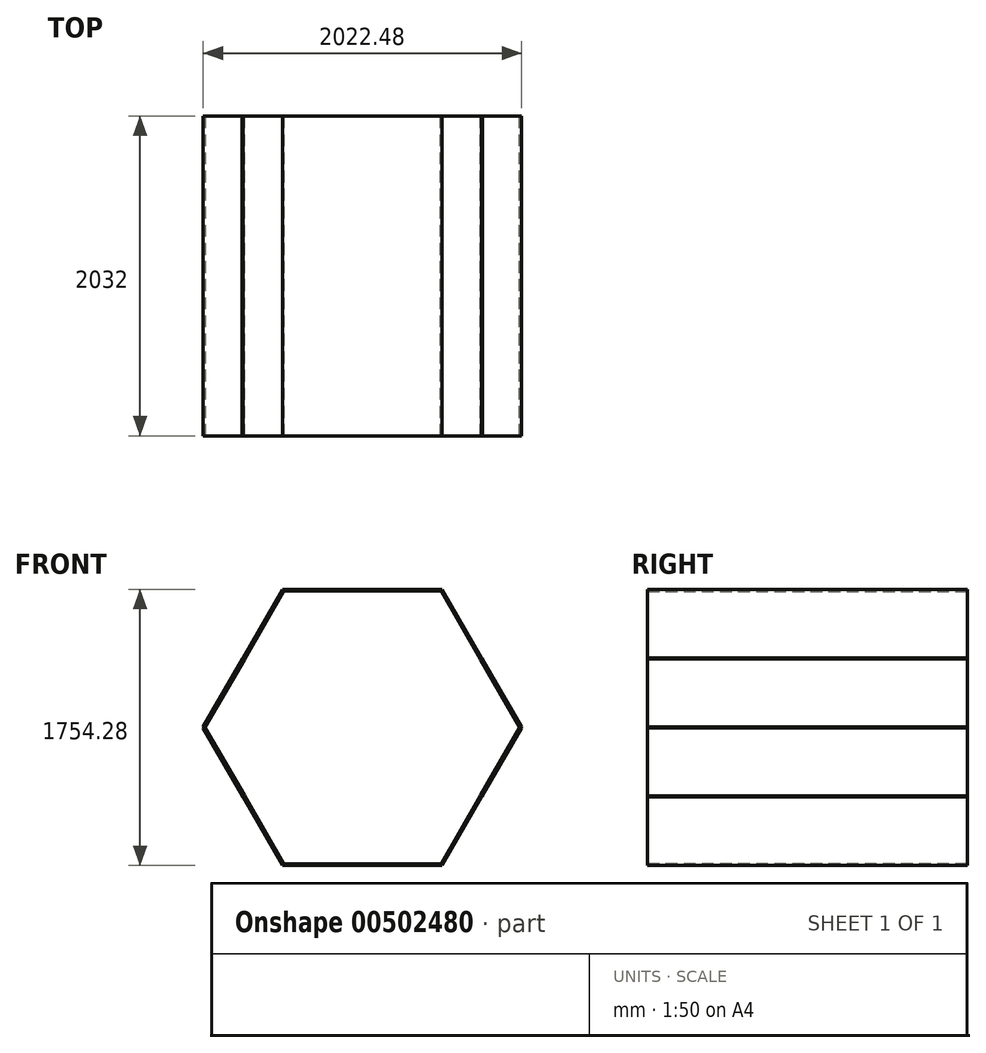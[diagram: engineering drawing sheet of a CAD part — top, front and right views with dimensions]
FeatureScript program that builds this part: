
annotation { "Feature Type Name" : "Feature", "Feature Type Description" : "" }
export const myFeature = defineFeature(function(context is Context, id is Id, definition is map)
    precondition{}
    {
        {
            var Q0;
            Q0=qCreatedBy(makeId("Front.planeOp"),FACE);
            var sketch = newSketch(context, id + "F0", { "sketchPlane" : qUnion([Q0])});
            skCircle(sketch, "E0.cCircle", {"center": v(0, 0) * mm, "radius": 866.03 * mm, "construction": true});
            skLineSegment(sketch, "E0.0", {"start": v(500, -866.03) * mm, "end": v(-500, -866.03) * mm});
            skLineSegment(sketch, "E0.1", {"start": v(-500, -866.03) * mm, "end": v(-1000, 0) * mm});
            skLineSegment(sketch, "E0.2", {"start": v(-1000, 0) * mm, "end": v(-500, 866.03) * mm});
            skLineSegment(sketch, "E0.3", {"start": v(-500, 866.03) * mm, "end": v(500, 866.03) * mm});
            skLineSegment(sketch, "E0.4", {"start": v(500, 866.03) * mm, "end": v(1000, 0) * mm});
            skLineSegment(sketch, "E0.5", {"start": v(1000, 0) * mm, "end": v(500, -866.03) * mm});
            skPoint(sketch, "E0.0.midPoint", {"position": v(0, -866.03) * mm});
            skCircle(sketch, "E1.cCircle", {"center": v(0, 0) * mm, "radius": 877.14 * mm, "construction": true});
            skLineSegment(sketch, "E1.0", {"start": v(506.42, -877.14) * mm, "end": v(-506.42, -877.14) * mm});
            skLineSegment(sketch, "E1.1", {"start": v(-506.42, -877.14) * mm, "end": v(-1012.83, 0) * mm});
            skLineSegment(sketch, "E1.2", {"start": v(-1012.83, 0) * mm, "end": v(-506.42, 877.14) * mm});
            skLineSegment(sketch, "E1.3", {"start": v(-506.42, 877.14) * mm, "end": v(506.42, 877.14) * mm});
            skLineSegment(sketch, "E1.4", {"start": v(506.42, 877.14) * mm, "end": v(1012.83, 0) * mm});
            skLineSegment(sketch, "E1.5", {"start": v(1012.83, 0) * mm, "end": v(506.42, -877.14) * mm});
            skPoint(sketch, "E1.0.midPoint", {"position": v(0, -877.14) * mm});
            skLineSegment(sketch, "E2", {"start": v(-506.42, 877.14) * mm, "end": v(-500, 866.03) * mm});
            skLineSegment(sketch, "E3", {"start": v(500, 866.03) * mm, "end": v(506.42, 877.14) * mm});
            skLineSegment(sketch, "E4", {"start": v(1000, 0) * mm, "end": v(1012.83, 0) * mm});
            skLineSegment(sketch, "E5", {"start": v(500, -866.03) * mm, "end": v(506.42, -877.14) * mm});
            skLineSegment(sketch, "E6", {"start": v(-506.42, -877.14) * mm, "end": v(-500, -866.03) * mm});
            skLineSegment(sketch, "E7", {"start": v(-1012.83, 0) * mm, "end": v(-1000, 0) * mm});
            skLineSegment(sketch, "E8", {"start": v(-759.62, 438.57) * mm, "end": v(-750, 433.01) * mm});
            skLineSegment(sketch, "E9", {"start": v(750, 433.01) * mm, "end": v(759.62, 438.57) * mm});
            skLineSegment(sketch, "E10", {"start": v(750, -433.01) * mm, "end": v(759.62, -438.57) * mm});
            skLineSegment(sketch, "E11", {"start": v(-759.62, -438.57) * mm, "end": v(-750, -433.01) * mm});
            skCircle(sketch, "E12", {"center": v(-759.62, 438.57) * mm, "radius": 3.18 * mm});
            skCircle(sketch, "E13", {"center": v(-759.62, -438.57) * mm, "radius": 3.18 * mm});
            skCircle(sketch, "E14", {"center": v(-1012.83, 0) * mm, "radius": 3.18 * mm});
            skCircle(sketch, "E15", {"center": v(-500, -866.03) * mm, "radius": 3.18 * mm});
            skCircle(sketch, "E16", {"center": v(500, -866.03) * mm, "radius": 3.18 * mm});
            skCircle(sketch, "E17", {"center": v(759.62, -438.57) * mm, "radius": 3.18 * mm});
            skCircle(sketch, "E18", {"center": v(1012.83, 0) * mm, "radius": 3.18 * mm});
            skCircle(sketch, "E19", {"center": v(759.62, 438.57) * mm, "radius": 3.18 * mm});
            skCircle(sketch, "E20", {"center": v(500, 866.03) * mm, "radius": 3.18 * mm});
            skCircle(sketch, "E21", {"center": v(-1000, 0) * mm, "radius": 3.18 * mm});
            skCircle(sketch, "E22", {"center": v(1000, 0) * mm, "radius": 3.18 * mm});
            skCircle(sketch, "E23", {"center": v(-500, 866.03) * mm, "radius": 3.18 * mm});
            skSolve(sketch);
        }
        {
            var Q0;
            {var subQ1=sQuery(id+"F0.wireOp",EDGE,"E1.0");Q0=makeQuery(id+"F0.imprint","IMPRINT",FACE,{"disambiguationData":[TD([[makeQuery(id+"F0.imprint","IMPRINT",EDGE,{"derivedFrom":subQ1}),-1.0]])]});}
            var Q1;
            {var subQ0=sQuery(id+"F0.wireOp",EDGE,"E10");var subQ1=sQuery(id+"F0.wireOp",EDGE,"E0.5");var subQ2=makeQuery(id+"F0.imprint","INTERSECT",VERTEX,{"derivedFrom":[subQ1,subQ0]});Q1=makeQuery(id+"F0.imprint","IMPRINT",FACE,{"disambiguationData":[TD([[makeQuery(id+"F0.imprint","IMPRINT",EDGE,{"disambiguationData":[TD([[subQ2,1.0]])],"derivedFrom":subQ1}),1.0]])]});}
            var Q2;
            {var subQ5=sQuery(id+"F0.wireOp",EDGE,"E9");var subQ6=sQuery(id+"F0.wireOp",EDGE,"E0.4");var subQ7=makeQuery(id+"F0.imprint","INTERSECT",VERTEX,{"derivedFrom":[subQ6,subQ5]});Q2=makeQuery(id+"F0.imprint","IMPRINT",FACE,{"disambiguationData":[TD([[makeQuery(id+"F0.imprint","IMPRINT",EDGE,{"disambiguationData":[TD([[subQ7,1.0]])],"derivedFrom":subQ6}),1.0]])]});}
            var Q3;
            {var subQ0=sQuery(id+"F0.wireOp",EDGE,"E11");var subQ1=sQuery(id+"F0.wireOp",EDGE,"E0.1");var subQ2=makeQuery(id+"F0.imprint","INTERSECT",VERTEX,{"derivedFrom":[subQ1,subQ0]});Q3=makeQuery(id+"F0.imprint","IMPRINT",FACE,{"disambiguationData":[TD([[makeQuery(id+"F0.imprint","IMPRINT",EDGE,{"disambiguationData":[TD([[subQ2,-1.0]])],"derivedFrom":subQ1}),1.0]])]});}
            var Q4;
            {var subQ5=sQuery(id+"F0.wireOp",EDGE,"E8");var subQ6=sQuery(id+"F0.wireOp",EDGE,"E0.2");var subQ7=makeQuery(id+"F0.imprint","INTERSECT",VERTEX,{"derivedFrom":[subQ6,subQ5]});Q4=makeQuery(id+"F0.imprint","IMPRINT",FACE,{"disambiguationData":[TD([[makeQuery(id+"F0.imprint","IMPRINT",EDGE,{"disambiguationData":[TD([[subQ7,-1.0]])],"derivedFrom":subQ6}),1.0]])]});}
            extrude(context, id + "F1", {"entities" : qUnion([Q0, Q1, Q2, Q3, Q4]), "depth" : 2032 * mm, "offsetDistance" : 25.4 * mm});
        }
        {
            var Q0;
            {var subQ0=sQuery(id+"F0.wireOp",EDGE,"E9");var subQ1=sQuery(id+"F0.wireOp",EDGE,"E0.4");var subQ2=makeQuery(id+"F0.imprint","INTERSECT",VERTEX,{"derivedFrom":[subQ1,subQ0]});Q0=makeQuery(id+"F0.imprint","IMPRINT",FACE,{"disambiguationData":[TD([[makeQuery(id+"F0.imprint","IMPRINT",EDGE,{"disambiguationData":[TD([[subQ2,-1.0]])],"derivedFrom":subQ1}),1.0]])]});}
            var Q1;
            {var subQ1=sQuery(id+"F0.wireOp",EDGE,"E1.3");Q1=makeQuery(id+"F0.imprint","IMPRINT",FACE,{"disambiguationData":[TD([[makeQuery(id+"F0.imprint","IMPRINT",EDGE,{"derivedFrom":subQ1}),-1.0]])]});}
            var Q2;
            {var subQ0=sQuery(id+"F0.wireOp",EDGE,"E8");var subQ1=sQuery(id+"F0.wireOp",EDGE,"E0.2");var subQ2=makeQuery(id+"F0.imprint","INTERSECT",VERTEX,{"derivedFrom":[subQ1,subQ0]});Q2=makeQuery(id+"F0.imprint","IMPRINT",FACE,{"disambiguationData":[TD([[makeQuery(id+"F0.imprint","IMPRINT",EDGE,{"disambiguationData":[TD([[subQ2,1.0]])],"derivedFrom":subQ1}),1.0]])]});}
            var Q3;
            {var subQ0=sQuery(id+"F0.wireOp",EDGE,"E11");var subQ1=sQuery(id+"F0.wireOp",EDGE,"E0.1");var subQ2=makeQuery(id+"F0.imprint","INTERSECT",VERTEX,{"derivedFrom":[subQ1,subQ0]});Q3=makeQuery(id+"F0.imprint","IMPRINT",FACE,{"disambiguationData":[TD([[makeQuery(id+"F0.imprint","IMPRINT",EDGE,{"disambiguationData":[TD([[subQ2,1.0]])],"derivedFrom":subQ1}),1.0]])]});}
            var Q4;
            {var subQ0=sQuery(id+"F0.wireOp",EDGE,"E10");var subQ1=sQuery(id+"F0.wireOp",EDGE,"E0.5");var subQ2=makeQuery(id+"F0.imprint","INTERSECT",VERTEX,{"derivedFrom":[subQ1,subQ0]});Q4=makeQuery(id+"F0.imprint","IMPRINT",FACE,{"disambiguationData":[TD([[makeQuery(id+"F0.imprint","IMPRINT",EDGE,{"disambiguationData":[TD([[subQ2,-1.0]])],"derivedFrom":subQ1}),1.0]])]});}
            extrude(context, id + "F2", {"entities" : qUnion([Q0, Q1, Q2, Q3, Q4]), "depth" : 2032 * mm, "offsetDistance" : 25.4 * mm});
        }
        {
            var Q0;
            {var subQ0=sQuery(id+"F0.wireOp",EDGE,"E1.1");var subQ1=makeQuery(id+"F0.imprint","INTERSECT",VERTEX,{"derivedFrom":[subQ0,sQuery(id+"F0.wireOp",EDGE,"E11")]});Q0=makeQuery(id+"F0.imprint","IMPRINT",FACE,{"disambiguationData":[TD([[makeQuery(id+"F0.imprint","IMPRINT",EDGE,{"disambiguationData":[TD([[subQ1,1.0]])],"derivedFrom":subQ0}),1.0]])]});}
            var Q1;
            {var subQ0=sQuery(id+"F0.wireOp",EDGE,"E11");var subQ1=sQuery(id+"F0.wireOp",EDGE,"E1.1");var subQ2=makeQuery(id+"F0.imprint","INTERSECT",VERTEX,{"derivedFrom":[subQ1,subQ0]});Q1=makeQuery(id+"F0.imprint","IMPRINT",FACE,{"disambiguationData":[TD([[makeQuery(id+"F0.imprint","IMPRINT",EDGE,{"disambiguationData":[TD([[subQ2,-1.0]])],"derivedFrom":subQ1}),-1.0]])]});}
            var Q2;
            {var subQ0=sQuery(id+"F0.wireOp",EDGE,"E11");var subQ1=sQuery(id+"F0.wireOp",EDGE,"E1.1");var subQ2=makeQuery(id+"F0.imprint","INTERSECT",VERTEX,{"derivedFrom":[subQ1,subQ0]});Q2=makeQuery(id+"F0.imprint","IMPRINT",FACE,{"disambiguationData":[TD([[makeQuery(id+"F0.imprint","IMPRINT",EDGE,{"disambiguationData":[TD([[subQ2,1.0]])],"derivedFrom":subQ1}),-1.0]])]});}
            var Q3;
            {var subQ1=sQuery(id+"F0.wireOp",EDGE,"E0.0");var subQ3=sQuery(id+"F0.wireOp",EDGE,"E15");var subQ4=makeQuery(id+"F0.imprint","INTERSECT",VERTEX,{"derivedFrom":[subQ1,subQ3]});Q3=makeQuery(id+"F0.imprint","IMPRINT",FACE,{"disambiguationData":[TD([[makeQuery(id+"F0.imprint","IMPRINT",EDGE,{"disambiguationData":[TD([[subQ4,-1.0]])],"derivedFrom":subQ3}),1.0]])]});}
            var Q4;
            {var subQ1=sQuery(id+"F0.wireOp",EDGE,"E0.0");var subQ3=sQuery(id+"F0.wireOp",EDGE,"E15");var subQ4=makeQuery(id+"F0.imprint","INTERSECT",VERTEX,{"derivedFrom":[subQ1,subQ3]});Q4=makeQuery(id+"F0.imprint","IMPRINT",FACE,{"disambiguationData":[TD([[makeQuery(id+"F0.imprint","IMPRINT",EDGE,{"disambiguationData":[TD([[subQ4,1.0]])],"derivedFrom":subQ3}),1.0]])]});}
            var Q5;
            {var subQ1=sQuery(id+"F0.wireOp",EDGE,"E0.1");var subQ3=sQuery(id+"F0.wireOp",EDGE,"E15");var subQ4=makeQuery(id+"F0.imprint","INTERSECT",VERTEX,{"derivedFrom":[subQ1,subQ3]});Q5=makeQuery(id+"F0.imprint","IMPRINT",FACE,{"disambiguationData":[TD([[makeQuery(id+"F0.imprint","IMPRINT",EDGE,{"disambiguationData":[TD([[subQ4,-1.0]])],"derivedFrom":subQ3}),1.0]])]});}
            var Q6;
            {var subQ1=sQuery(id+"F0.wireOp",EDGE,"E0.5");var subQ3=sQuery(id+"F0.wireOp",EDGE,"E16");var subQ4=makeQuery(id+"F0.imprint","INTERSECT",VERTEX,{"derivedFrom":[subQ1,subQ3]});Q6=makeQuery(id+"F0.imprint","IMPRINT",FACE,{"disambiguationData":[TD([[makeQuery(id+"F0.imprint","IMPRINT",EDGE,{"disambiguationData":[TD([[subQ4,1.0]])],"derivedFrom":subQ3}),1.0]])]});}
            var Q7;
            {var subQ1=sQuery(id+"F0.wireOp",EDGE,"E0.0");var subQ3=sQuery(id+"F0.wireOp",EDGE,"E16");var subQ4=makeQuery(id+"F0.imprint","INTERSECT",VERTEX,{"derivedFrom":[subQ1,subQ3]});Q7=makeQuery(id+"F0.imprint","IMPRINT",FACE,{"disambiguationData":[TD([[makeQuery(id+"F0.imprint","IMPRINT",EDGE,{"disambiguationData":[TD([[subQ4,1.0]])],"derivedFrom":subQ3}),1.0]])]});}
            var Q8;
            {var subQ1=sQuery(id+"F0.wireOp",EDGE,"E0.0");var subQ3=sQuery(id+"F0.wireOp",EDGE,"E16");var subQ4=makeQuery(id+"F0.imprint","INTERSECT",VERTEX,{"derivedFrom":[subQ1,subQ3]});Q8=makeQuery(id+"F0.imprint","IMPRINT",FACE,{"disambiguationData":[TD([[makeQuery(id+"F0.imprint","IMPRINT",EDGE,{"disambiguationData":[TD([[subQ4,-1.0]])],"derivedFrom":subQ3}),1.0]])]});}
            var Q9;
            {var subQ0=sQuery(id+"F0.wireOp",EDGE,"E10");var subQ1=sQuery(id+"F0.wireOp",EDGE,"E1.5");var subQ2=makeQuery(id+"F0.imprint","INTERSECT",VERTEX,{"derivedFrom":[subQ1,subQ0]});Q9=makeQuery(id+"F0.imprint","IMPRINT",FACE,{"disambiguationData":[TD([[makeQuery(id+"F0.imprint","IMPRINT",EDGE,{"disambiguationData":[TD([[subQ2,1.0]])],"derivedFrom":subQ1}),-1.0]])]});}
            var Q10;
            {var subQ0=sQuery(id+"F0.wireOp",EDGE,"E10");var subQ1=sQuery(id+"F0.wireOp",EDGE,"E1.5");var subQ2=makeQuery(id+"F0.imprint","INTERSECT",VERTEX,{"derivedFrom":[subQ1,subQ0]});Q10=makeQuery(id+"F0.imprint","IMPRINT",FACE,{"disambiguationData":[TD([[makeQuery(id+"F0.imprint","IMPRINT",EDGE,{"disambiguationData":[TD([[subQ2,-1.0]])],"derivedFrom":subQ1}),-1.0]])]});}
            var Q11;
            {var subQ0=sQuery(id+"F0.wireOp",EDGE,"E1.5");var subQ1=makeQuery(id+"F0.imprint","INTERSECT",VERTEX,{"derivedFrom":[subQ0,sQuery(id+"F0.wireOp",EDGE,"E10")]});Q11=makeQuery(id+"F0.imprint","IMPRINT",FACE,{"disambiguationData":[TD([[makeQuery(id+"F0.imprint","IMPRINT",EDGE,{"disambiguationData":[TD([[subQ1,1.0]])],"derivedFrom":subQ0}),1.0]])]});}
            var Q12;
            {var subQ1=sQuery(id+"F0.wireOp",EDGE,"E0.4");var subQ3=sQuery(id+"F0.wireOp",EDGE,"E22");var subQ4=makeQuery(id+"F0.imprint","INTERSECT",VERTEX,{"derivedFrom":[subQ1,subQ3]});Q12=makeQuery(id+"F0.imprint","IMPRINT",FACE,{"disambiguationData":[TD([[makeQuery(id+"F0.imprint","IMPRINT",EDGE,{"disambiguationData":[TD([[subQ4,1.0]])],"derivedFrom":subQ3}),1.0]])]});}
            var Q13;
            {var subQ1=sQuery(id+"F0.wireOp",EDGE,"E0.5");var subQ3=sQuery(id+"F0.wireOp",EDGE,"E22");var subQ4=makeQuery(id+"F0.imprint","INTERSECT",VERTEX,{"derivedFrom":[subQ1,subQ3]});Q13=makeQuery(id+"F0.imprint","IMPRINT",FACE,{"disambiguationData":[TD([[makeQuery(id+"F0.imprint","IMPRINT",EDGE,{"disambiguationData":[TD([[subQ4,-1.0]])],"derivedFrom":subQ3}),1.0]])]});}
            var Q14;
            {var subQ1=sQuery(id+"F0.wireOp",EDGE,"E0.4");var subQ3=sQuery(id+"F0.wireOp",EDGE,"E22");var subQ4=makeQuery(id+"F0.imprint","INTERSECT",VERTEX,{"derivedFrom":[subQ1,subQ3]});Q14=makeQuery(id+"F0.imprint","IMPRINT",FACE,{"disambiguationData":[TD([[makeQuery(id+"F0.imprint","IMPRINT",EDGE,{"disambiguationData":[TD([[subQ4,-1.0]])],"derivedFrom":subQ3}),1.0]])]});}
            var Q15;
            {var subQ0=sQuery(id+"F0.wireOp",EDGE,"E1.4");var subQ1=makeQuery(id+"F0.imprint","INTERSECT",VERTEX,{"derivedFrom":[subQ0,sQuery(id+"F0.wireOp",EDGE,"E9")]});Q15=makeQuery(id+"F0.imprint","IMPRINT",FACE,{"disambiguationData":[TD([[makeQuery(id+"F0.imprint","IMPRINT",EDGE,{"disambiguationData":[TD([[subQ1,1.0]])],"derivedFrom":subQ0}),1.0]])]});}
            var Q16;
            {var subQ0=sQuery(id+"F0.wireOp",EDGE,"E9");var subQ1=sQuery(id+"F0.wireOp",EDGE,"E1.4");var subQ2=makeQuery(id+"F0.imprint","INTERSECT",VERTEX,{"derivedFrom":[subQ1,subQ0]});Q16=makeQuery(id+"F0.imprint","IMPRINT",FACE,{"disambiguationData":[TD([[makeQuery(id+"F0.imprint","IMPRINT",EDGE,{"disambiguationData":[TD([[subQ2,-1.0]])],"derivedFrom":subQ1}),-1.0]])]});}
            var Q17;
            {var subQ0=sQuery(id+"F0.wireOp",EDGE,"E9");var subQ1=sQuery(id+"F0.wireOp",EDGE,"E1.4");var subQ2=makeQuery(id+"F0.imprint","INTERSECT",VERTEX,{"derivedFrom":[subQ1,subQ0]});Q17=makeQuery(id+"F0.imprint","IMPRINT",FACE,{"disambiguationData":[TD([[makeQuery(id+"F0.imprint","IMPRINT",EDGE,{"disambiguationData":[TD([[subQ2,1.0]])],"derivedFrom":subQ1}),-1.0]])]});}
            var Q18;
            {var subQ1=sQuery(id+"F0.wireOp",EDGE,"E0.3");var subQ3=sQuery(id+"F0.wireOp",EDGE,"E20");var subQ4=makeQuery(id+"F0.imprint","INTERSECT",VERTEX,{"derivedFrom":[subQ1,subQ3]});Q18=makeQuery(id+"F0.imprint","IMPRINT",FACE,{"disambiguationData":[TD([[makeQuery(id+"F0.imprint","IMPRINT",EDGE,{"disambiguationData":[TD([[subQ4,1.0]])],"derivedFrom":subQ3}),1.0]])]});}
            var Q19;
            {var subQ1=sQuery(id+"F0.wireOp",EDGE,"E0.3");var subQ3=sQuery(id+"F0.wireOp",EDGE,"E20");var subQ4=makeQuery(id+"F0.imprint","INTERSECT",VERTEX,{"derivedFrom":[subQ1,subQ3]});Q19=makeQuery(id+"F0.imprint","IMPRINT",FACE,{"disambiguationData":[TD([[makeQuery(id+"F0.imprint","IMPRINT",EDGE,{"disambiguationData":[TD([[subQ4,-1.0]])],"derivedFrom":subQ3}),1.0]])]});}
            var Q20;
            {var subQ1=sQuery(id+"F0.wireOp",EDGE,"E0.4");var subQ3=sQuery(id+"F0.wireOp",EDGE,"E20");var subQ4=makeQuery(id+"F0.imprint","INTERSECT",VERTEX,{"derivedFrom":[subQ1,subQ3]});Q20=makeQuery(id+"F0.imprint","IMPRINT",FACE,{"disambiguationData":[TD([[makeQuery(id+"F0.imprint","IMPRINT",EDGE,{"disambiguationData":[TD([[subQ4,-1.0]])],"derivedFrom":subQ3}),1.0]])]});}
            var Q21;
            {var subQ1=sQuery(id+"F0.wireOp",EDGE,"E0.2");var subQ3=sQuery(id+"F0.wireOp",EDGE,"E23");var subQ4=makeQuery(id+"F0.imprint","INTERSECT",VERTEX,{"derivedFrom":[subQ1,subQ3]});Q21=makeQuery(id+"F0.imprint","IMPRINT",FACE,{"disambiguationData":[TD([[makeQuery(id+"F0.imprint","IMPRINT",EDGE,{"disambiguationData":[TD([[subQ4,-1.0]])],"derivedFrom":subQ3}),1.0]])]});}
            var Q22;
            {var subQ1=sQuery(id+"F0.wireOp",EDGE,"E0.3");var subQ3=sQuery(id+"F0.wireOp",EDGE,"E23");var subQ4=makeQuery(id+"F0.imprint","INTERSECT",VERTEX,{"derivedFrom":[subQ1,subQ3]});Q22=makeQuery(id+"F0.imprint","IMPRINT",FACE,{"disambiguationData":[TD([[makeQuery(id+"F0.imprint","IMPRINT",EDGE,{"disambiguationData":[TD([[subQ4,-1.0]])],"derivedFrom":subQ3}),1.0]])]});}
            var Q23;
            {var subQ1=sQuery(id+"F0.wireOp",EDGE,"E0.2");var subQ3=sQuery(id+"F0.wireOp",EDGE,"E23");var subQ4=makeQuery(id+"F0.imprint","INTERSECT",VERTEX,{"derivedFrom":[subQ1,subQ3]});Q23=makeQuery(id+"F0.imprint","IMPRINT",FACE,{"disambiguationData":[TD([[makeQuery(id+"F0.imprint","IMPRINT",EDGE,{"disambiguationData":[TD([[subQ4,1.0]])],"derivedFrom":subQ3}),1.0]])]});}
            var Q24;
            {var subQ0=sQuery(id+"F0.wireOp",EDGE,"E8");var subQ1=sQuery(id+"F0.wireOp",EDGE,"E1.2");var subQ2=makeQuery(id+"F0.imprint","INTERSECT",VERTEX,{"derivedFrom":[subQ1,subQ0]});Q24=makeQuery(id+"F0.imprint","IMPRINT",FACE,{"disambiguationData":[TD([[makeQuery(id+"F0.imprint","IMPRINT",EDGE,{"disambiguationData":[TD([[subQ2,-1.0]])],"derivedFrom":subQ1}),-1.0]])]});}
            var Q25;
            {var subQ0=sQuery(id+"F0.wireOp",EDGE,"E1.2");var subQ1=makeQuery(id+"F0.imprint","INTERSECT",VERTEX,{"derivedFrom":[subQ0,sQuery(id+"F0.wireOp",EDGE,"E8")]});Q25=makeQuery(id+"F0.imprint","IMPRINT",FACE,{"disambiguationData":[TD([[makeQuery(id+"F0.imprint","IMPRINT",EDGE,{"disambiguationData":[TD([[subQ1,1.0]])],"derivedFrom":subQ0}),1.0]])]});}
            var Q26;
            {var subQ0=sQuery(id+"F0.wireOp",EDGE,"E8");var subQ1=sQuery(id+"F0.wireOp",EDGE,"E1.2");var subQ2=makeQuery(id+"F0.imprint","INTERSECT",VERTEX,{"derivedFrom":[subQ1,subQ0]});Q26=makeQuery(id+"F0.imprint","IMPRINT",FACE,{"disambiguationData":[TD([[makeQuery(id+"F0.imprint","IMPRINT",EDGE,{"disambiguationData":[TD([[subQ2,1.0]])],"derivedFrom":subQ1}),-1.0]])]});}
            var Q27;
            {var subQ1=sQuery(id+"F0.wireOp",EDGE,"E0.1");var subQ3=sQuery(id+"F0.wireOp",EDGE,"E21");var subQ4=makeQuery(id+"F0.imprint","INTERSECT",VERTEX,{"derivedFrom":[subQ1,subQ3]});Q27=makeQuery(id+"F0.imprint","IMPRINT",FACE,{"disambiguationData":[TD([[makeQuery(id+"F0.imprint","IMPRINT",EDGE,{"disambiguationData":[TD([[subQ4,-1.0]])],"derivedFrom":subQ3}),1.0]])]});}
            var Q28;
            {var subQ1=sQuery(id+"F0.wireOp",EDGE,"E0.2");var subQ3=sQuery(id+"F0.wireOp",EDGE,"E21");var subQ4=makeQuery(id+"F0.imprint","INTERSECT",VERTEX,{"derivedFrom":[subQ1,subQ3]});Q28=makeQuery(id+"F0.imprint","IMPRINT",FACE,{"disambiguationData":[TD([[makeQuery(id+"F0.imprint","IMPRINT",EDGE,{"disambiguationData":[TD([[subQ4,-1.0]])],"derivedFrom":subQ3}),1.0]])]});}
            var Q29;
            {var subQ1=sQuery(id+"F0.wireOp",EDGE,"E0.1");var subQ3=sQuery(id+"F0.wireOp",EDGE,"E21");var subQ4=makeQuery(id+"F0.imprint","INTERSECT",VERTEX,{"derivedFrom":[subQ1,subQ3]});Q29=makeQuery(id+"F0.imprint","IMPRINT",FACE,{"disambiguationData":[TD([[makeQuery(id+"F0.imprint","IMPRINT",EDGE,{"disambiguationData":[TD([[subQ4,1.0]])],"derivedFrom":subQ3}),1.0]])]});}
            extrude(context, id + "F3", {"entities" : qUnion([Q0, Q1, Q2, Q3, Q4, Q5, Q6, Q7, Q8, Q9, Q10, Q11, Q12, Q13, Q14, Q15, Q16, Q17, Q18, Q19, Q20, Q21, Q22, Q23, Q24, Q25, Q26, Q27, Q28, Q29]), "depth" : 2032 * mm, "offsetDistance" : 25.4 * mm});
        }
    });
